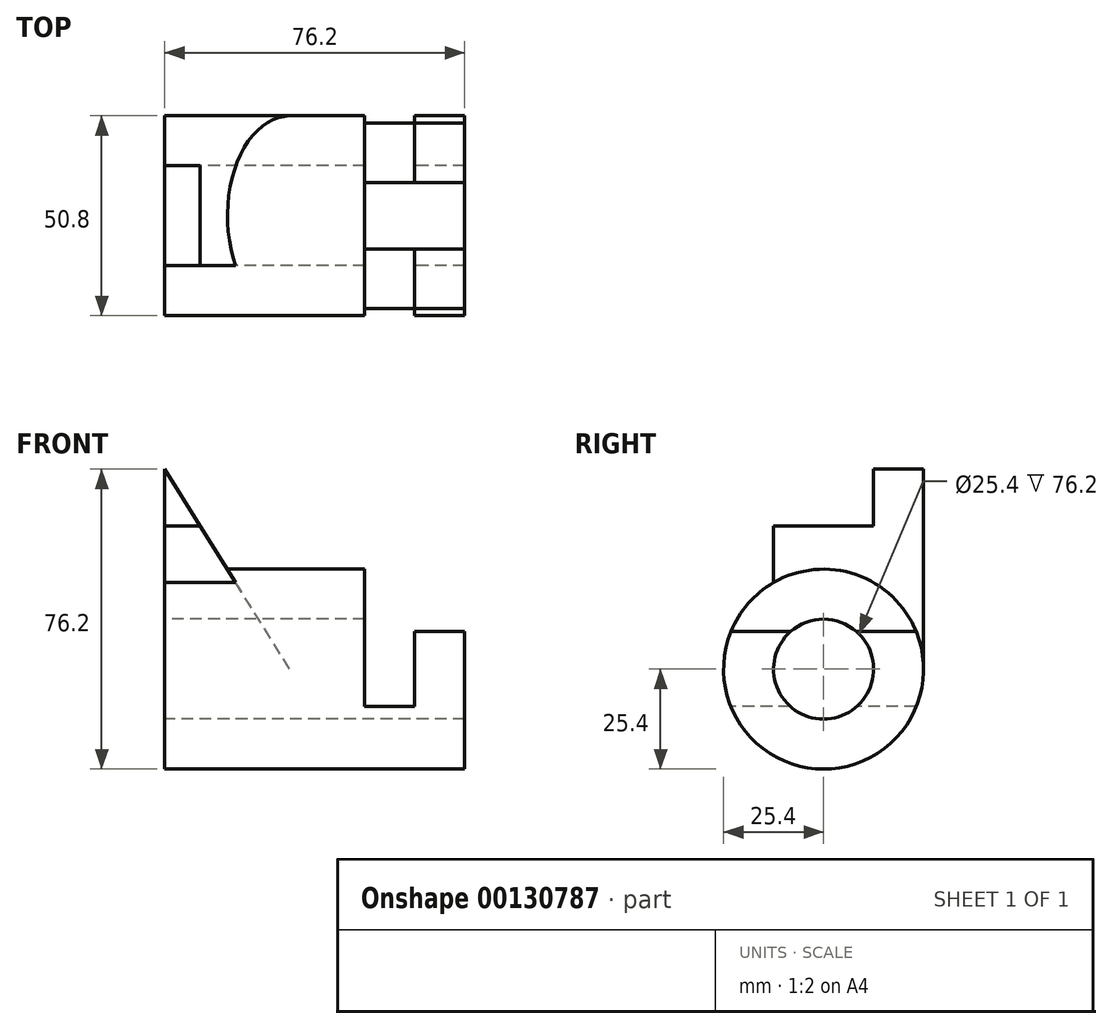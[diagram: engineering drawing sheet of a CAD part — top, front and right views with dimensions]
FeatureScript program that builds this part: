
annotation { "Feature Type Name" : "Feature", "Feature Type Description" : "" }
export const myFeature = defineFeature(function(context is Context, id is Id, definition is map)
    precondition{}
    {
        {
            var Q0;
            Q0=qCreatedBy(makeId("Right.planeOp"),FACE);
            var sketch = newSketch(context, id + "F0", { "sketchPlane" : qUnion([Q0])});
            skCircle(sketch, "E0", {"center": v(0, 0) * mm, "radius": 12.7 * mm});
            skCircle(sketch, "E1", {"center": v(0, 0) * mm, "radius": 25.4 * mm});
            skSolve(sketch);
        }
        {
            var Q0;
            Q0=makeQuery(id+"F0.imprint","IMPRINT",FACE,{"disambiguationData":[TD([[makeQuery(id+"F0.imprint","IMPRINT",EDGE,{"derivedFrom":sQuery(id+"F0.wireOp",EDGE,"E0")}),-1.0]])]});
            extrude(context, id + "F1", {"entities" : qUnion([Q0]), "depth" : 76.2 * mm});
        }
        {
            var Q0;
            Q0=qCreatedBy(makeId("Front.planeOp"),FACE);
            var sketch = newSketch(context, id + "F2", { "sketchPlane" : qUnion([Q0])});
            skLineSegment(sketch, "E2", {"start": v(0, 25.4) * mm, "end": v(76.2, 25.4) * mm});
            skLineSegment(sketch, "E3", {"start": v(76.2, -25.4) * mm, "end": v(0, -25.4) * mm});
            skLineSegment(sketch, "E4.0", {"start": v(76.2, 25.4) * mm, "end": v(76.2, -25.4) * mm});
            skLineSegment(sketch, "E5", {"start": v(50.8, 25.4) * mm, "end": v(50.8, -9.53) * mm});
            skLineSegment(sketch, "E6", {"start": v(50.8, -9.53) * mm, "end": v(63.5, -9.52) * mm});
            skLineSegment(sketch, "E7", {"start": v(63.5, -9.53) * mm, "end": v(63.5, 9.53) * mm});
            skLineSegment(sketch, "E8", {"start": v(63.5, 9.53) * mm, "end": v(76.2, 9.53) * mm});
            skLineSegment(sketch, "E9", {"start": v(76.2, 9.53) * mm, "end": v(76.2, 25.4) * mm});
            skLineSegment(sketch, "E10", {"start": v(50.8, 25.4) * mm, "end": v(76.2, 25.4) * mm});
            skSolve(sketch);
        }
        {
            var Q0;
            Q0 = qSketchRegion(id + "F2", true);
            extrude(context, id + "F3", {"entities" : qUnion([Q0]), "operationType" : NewBodyOperationType.REMOVE, "endBound" : BoundingType.THROUGH_ALL, "oppositeDirection" : true, "depth" : 25.4 * mm, "hasSecondDirection" : true, "secondDirectionOppositeDirection" : false, "secondDirectionDepth" : 25.4 * mm});
        }
        {
            var Q0;
            Q0=qCreatedBy(makeId("Front.planeOp"),FACE);
            var sketch = newSketch(context, id + "F4", { "sketchPlane" : qUnion([Q0])});
            skLineSegment(sketch, "E11", {"start": v(0, 50.8) * mm, "end": v(0, 0) * mm});
            skLineSegment(sketch, "E12", {"start": v(0, 0) * mm, "end": v(31.75, 0) * mm});
            skLineSegment(sketch, "E13", {"start": v(31.75, 0) * mm, "end": v(0, 50.8) * mm});
            skSolve(sketch);
        }
        {
            var Q0;
            Q0 = qSketchRegion(id + "F4", true);
            extrude(context, id + "F5", {"entities" : qUnion([Q0]), "operationType" : NewBodyOperationType.ADD, "oppositeDirection" : true, "depth" : 25.4 * mm, "hasSecondDirection" : true, "secondDirectionOppositeDirection" : false, "secondDirectionDepth" : 12.7 * mm});
        }
        {
            var Q0;
            Q0=makeQuery(id+"F5.boolean.opBoolean","MERGE",FACE,{"derivedFrom":[makeQuery(id+"F1.opExtrude","CAP_FACE",FACE,{"disambiguationData":[OSD([sQuery(id+"F0.wireOp",EDGE,"E0"),sQuery(id+"F0.wireOp",EDGE,"E1")])],"isStart":true}),makeQuery(id+"F5.opExtrude","SWEPT_FACE",FACE,{"disambiguationData":[OSD([sQuery(id+"F4.wireOp",EDGE,"E11")])]})]});
            var sketch = newSketch(context, id + "F6", { "sketchPlane" : qUnion([Q0])});
            skLineSegment(sketch, "E14.bottom", {"start": v(-12.7, 50.8) * mm, "end": v(12.7, 50.8) * mm});
            skLineSegment(sketch, "E14.top", {"start": v(-12.7, 36.4) * mm, "end": v(12.7, 36.4) * mm});
            skLineSegment(sketch, "E14.left", {"start": v(-12.7, 50.8) * mm, "end": v(-12.7, 36.4) * mm});
            skLineSegment(sketch, "E14.right", {"start": v(12.7, 50.8) * mm, "end": v(12.7, 36.4) * mm});
            skSolve(sketch);
        }
        {
            var Q0;
            Q0=makeQuery(id+"F6.imprint","IMPRINT",FACE,{"disambiguationData":[TD([[makeQuery(id+"F6.imprint","IMPRINT",EDGE,{"derivedFrom":sQuery(id+"F6.wireOp",EDGE,"E14.bottom")}),-1.0]])]});
            extrude(context, id + "F7", {"entities" : qUnion([Q0]), "operationType" : NewBodyOperationType.REMOVE, "endBound" : BoundingType.THROUGH_ALL, "oppositeDirection" : true, "depth" : 25.4 * mm});
        }
        {
            var Q0;
            Q0=makeQuery(id+"F0.imprint","IMPRINT",FACE,{"disambiguationData":[TD([[makeQuery(id+"F0.imprint","IMPRINT",EDGE,{"derivedFrom":sQuery(id+"F0.wireOp",EDGE,"E0")}),1.0]])]});
            extrude(context, id + "F8", {"entities" : qUnion([Q0]), "operationType" : NewBodyOperationType.REMOVE, "endBound" : BoundingType.THROUGH_ALL, "depth" : 25.4 * mm});
        }
    });
